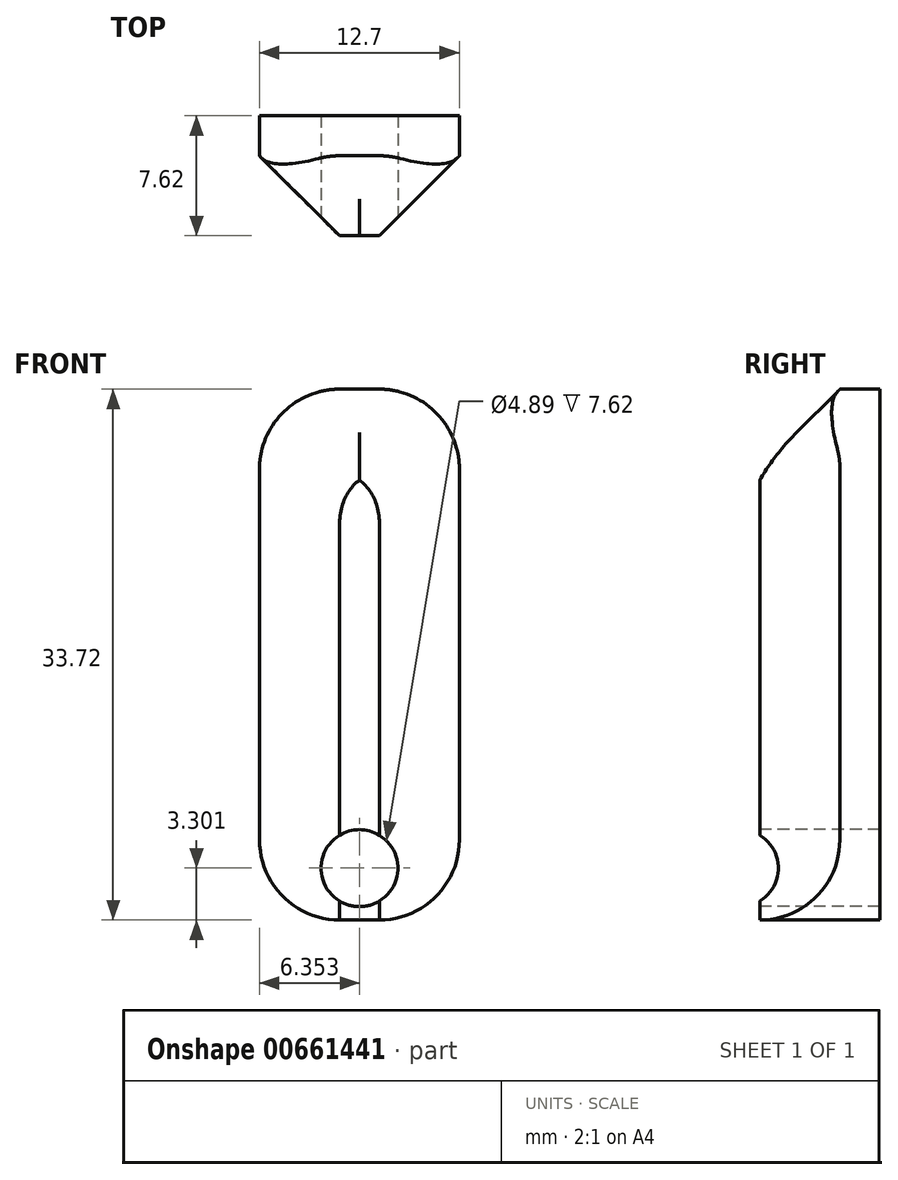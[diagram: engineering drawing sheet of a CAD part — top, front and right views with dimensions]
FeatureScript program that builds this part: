
annotation { "Feature Type Name" : "Feature", "Feature Type Description" : "" }
export const myFeature = defineFeature(function(context is Context, id is Id, definition is map)
    precondition{}
    {
        {
            var Q0;
            Q0=qCreatedBy(makeId("Front.planeOp"),FACE);
            var sketch = newSketch(context, id + "F0", { "sketchPlane" : qUnion([Q0])});
            skLineSegment(sketch, "E0.bottom", {"start": v(-34.89, 19.21) * mm, "end": v(-22.19, 19.21) * mm});
            skLineSegment(sketch, "E0.top", {"start": v(-34.89, -14.5) * mm, "end": v(-22.19, -14.5) * mm});
            skLineSegment(sketch, "E0.left", {"start": v(-34.89, 19.21) * mm, "end": v(-34.89, -14.5) * mm});
            skLineSegment(sketch, "E0.right", {"start": v(-22.19, 19.21) * mm, "end": v(-22.19, -14.5) * mm});
            skSolve(sketch);
        }
        {
            var Q0;
            Q0 = qSketchRegion(id + "F0", true);
            extrude(context, id + "F1", {"entities" : qUnion([Q0]), "depth" : 7.62 * mm, "offsetDistance" : 25.4 * mm});
        }
        {
            var Q0;
            Q0=makeQuery(id+"F1.opExtrude","CAP_FACE",FACE,{"disambiguationData":[OSD([sQuery(id+"F0.wireOp",EDGE,"E0.bottom"),sQuery(id+"F0.wireOp",EDGE,"E0.top"),sQuery(id+"F0.wireOp",EDGE,"E0.left"),sQuery(id+"F0.wireOp",EDGE,"E0.right")])],"isStart":false});
            var sketch = newSketch(context, id + "F2", { "sketchPlane" : qUnion([Q0])});
            skLineSegment(sketch, "E1", {"start": v(-28.54, -14.5) * mm, "end": v(-28.54, 19.21) * mm});
            skCircle(sketch, "E2", {"center": v(-28.54, -11.2) * mm, "radius": 2.45 * mm});
            skSolve(sketch);
        }
        {
            var Q0;
            Q0 = qSketchRegion(id + "F2", true);
            extrude(context, id + "F3", {"entities" : qUnion([Q0]), "operationType" : NewBodyOperationType.REMOVE, "oppositeDirection" : true, "depth" : 25.4 * mm, "offsetDistance" : 25.4 * mm});
        }
        {
            var Q0;
            Q0=makeQuery(id+"F1.opExtrude","CAP_EDGE",EDGE,{"disambiguationData":[OSD([sQuery(id+"F0.wireOp",EDGE,"E0.right")])],"isStart":false});
            var Q1;
            Q1=makeQuery(id+"F1.opExtrude","CAP_EDGE",EDGE,{"disambiguationData":[OSD([sQuery(id+"F0.wireOp",EDGE,"E0.left")])],"isStart":false});
            var Q2;
            Q2=makeQuery(id+"F1.opExtrude","CAP_EDGE",EDGE,{"disambiguationData":[OSD([sQuery(id+"F0.wireOp",EDGE,"E0.bottom")])],"isStart":false});
            chamfer(context, id + "F4", {"entities" : qUnion([Q0, Q1, Q2]), "width" : 5.08 * mm, "tangentPropagation" : true});
        }
        {
            var Q0;
            Q0=makeQuery(id+"F1.opExtrude","SWEPT_EDGE",EDGE,{"disambiguationData":[OSD([sQuery(id+"F0.wireOp",EDGE,"E0.bottom"),sQuery(id+"F0.wireOp",EDGE,"E0.left")])]});
            var Q1;
            Q1=makeQuery(id+"F1.opExtrude","SWEPT_EDGE",EDGE,{"disambiguationData":[OSD([sQuery(id+"F0.wireOp",EDGE,"E0.bottom"),sQuery(id+"F0.wireOp",EDGE,"E0.right")])]});
            var Q2;
            Q2=makeQuery(id+"F1.opExtrude","SWEPT_EDGE",EDGE,{"disambiguationData":[OSD([sQuery(id+"F0.wireOp",EDGE,"E0.top"),sQuery(id+"F0.wireOp",EDGE,"E0.right")])]});
            var Q3;
            Q3=makeQuery(id+"F1.opExtrude","SWEPT_EDGE",EDGE,{"disambiguationData":[OSD([sQuery(id+"F0.wireOp",EDGE,"E0.top"),sQuery(id+"F0.wireOp",EDGE,"E0.left")])]});
            var Q4;
            Q4=makeQuery(id+"F4.opChamfer","BLEND_EDGE",EDGE,{"blendedFrom":[makeQuery(id+"F1.opExtrude","CAP_EDGE",EDGE,{"disambiguationData":[OSD([sQuery(id+"F0.wireOp",EDGE,"E0.bottom")])],"isStart":false}),makeQuery(id+"F1.opExtrude","CAP_EDGE",EDGE,{"disambiguationData":[OSD([sQuery(id+"F0.wireOp",EDGE,"E0.right")])],"isStart":false})],"blendedInto":[]});
            var Q5;
            Q5=makeQuery(id+"F4.opChamfer","BLEND_EDGE",EDGE,{"blendedFrom":[makeQuery(id+"F1.opExtrude","CAP_EDGE",EDGE,{"disambiguationData":[OSD([sQuery(id+"F0.wireOp",EDGE,"E0.bottom")])],"isStart":false}),makeQuery(id+"F1.opExtrude","CAP_EDGE",EDGE,{"disambiguationData":[OSD([sQuery(id+"F0.wireOp",EDGE,"E0.left")])],"isStart":false})],"blendedInto":[]});
            fillet(context, id + "F5", {"entities" : qUnion([Q0, Q1, Q2, Q3, Q4, Q5]), "radius" : 5.08 * mm, "tangentPropagation" : true, "allowEdgeOverflow" : false});
        }
    });
